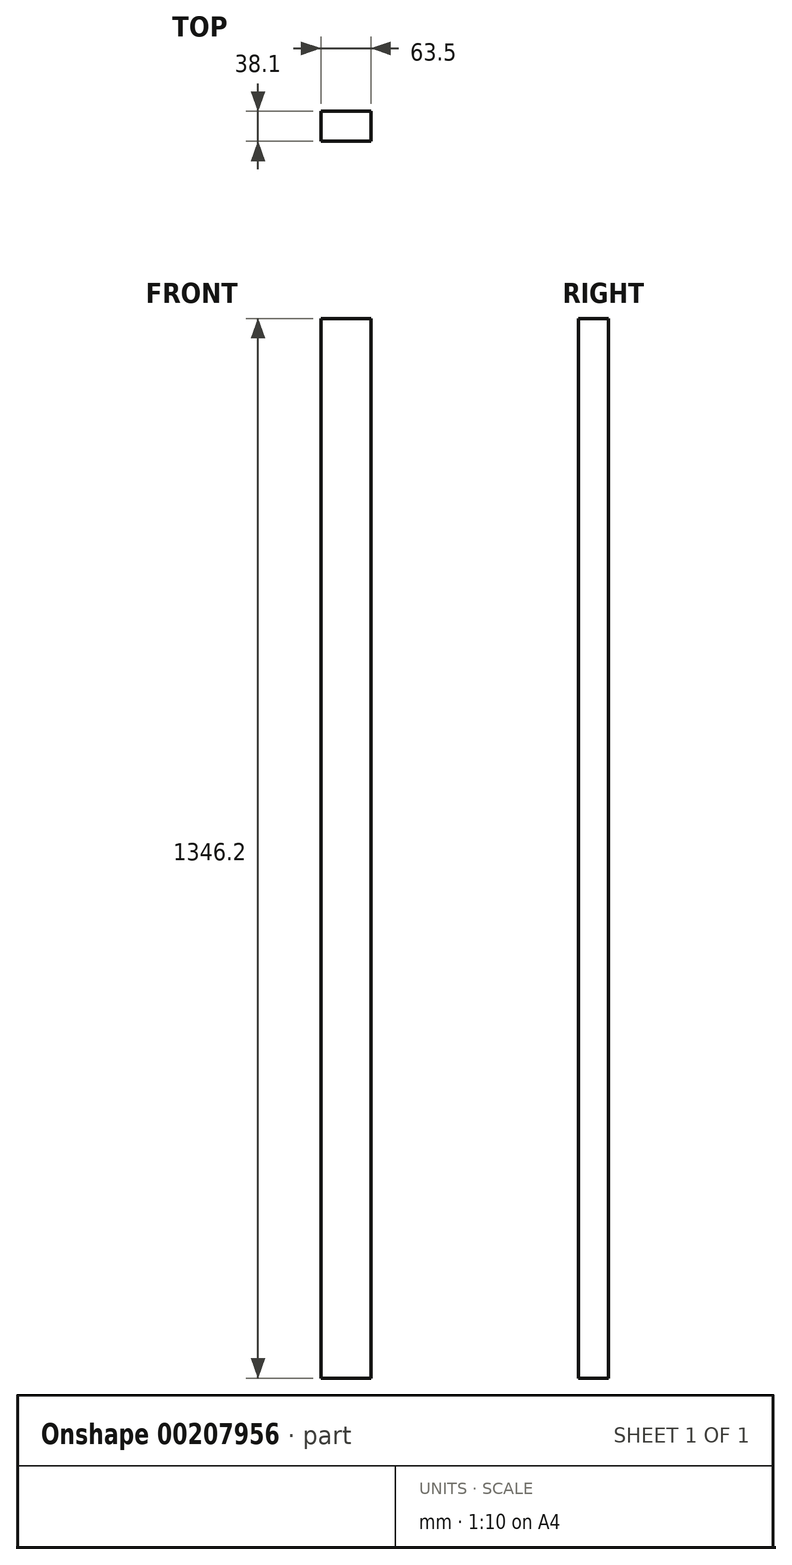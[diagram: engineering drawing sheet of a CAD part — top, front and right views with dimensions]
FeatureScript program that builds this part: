
annotation { "Feature Type Name" : "Feature", "Feature Type Description" : "" }
export const myFeature = defineFeature(function(context is Context, id is Id, definition is map)
    precondition{}
    {
        {
            var Q0;
            Q0=qCreatedBy(makeId("Top.planeOp"),FACE);
            var sketch = newSketch(context, id + "F0", { "sketchPlane" : qUnion([Q0])});
            skLineSegment(sketch, "E0.bottom", {"start": v(0, 0) * mm, "end": v(63.5, 0) * mm});
            skLineSegment(sketch, "E0.top", {"start": v(0, 38.1) * mm, "end": v(63.5, 38.1) * mm});
            skLineSegment(sketch, "E0.left", {"start": v(0, 0) * mm, "end": v(0, 38.1) * mm});
            skLineSegment(sketch, "E0.right", {"start": v(63.5, 0) * mm, "end": v(63.5, 38.1) * mm});
            skSolve(sketch);
        }
        {
            var Q0;
            Q0 = qSketchRegion(id + "F0", true);
            extrude(context, id + "F1", {"entities" : qUnion([Q0]), "depth" : 1346.2 * mm});
        }
    });
